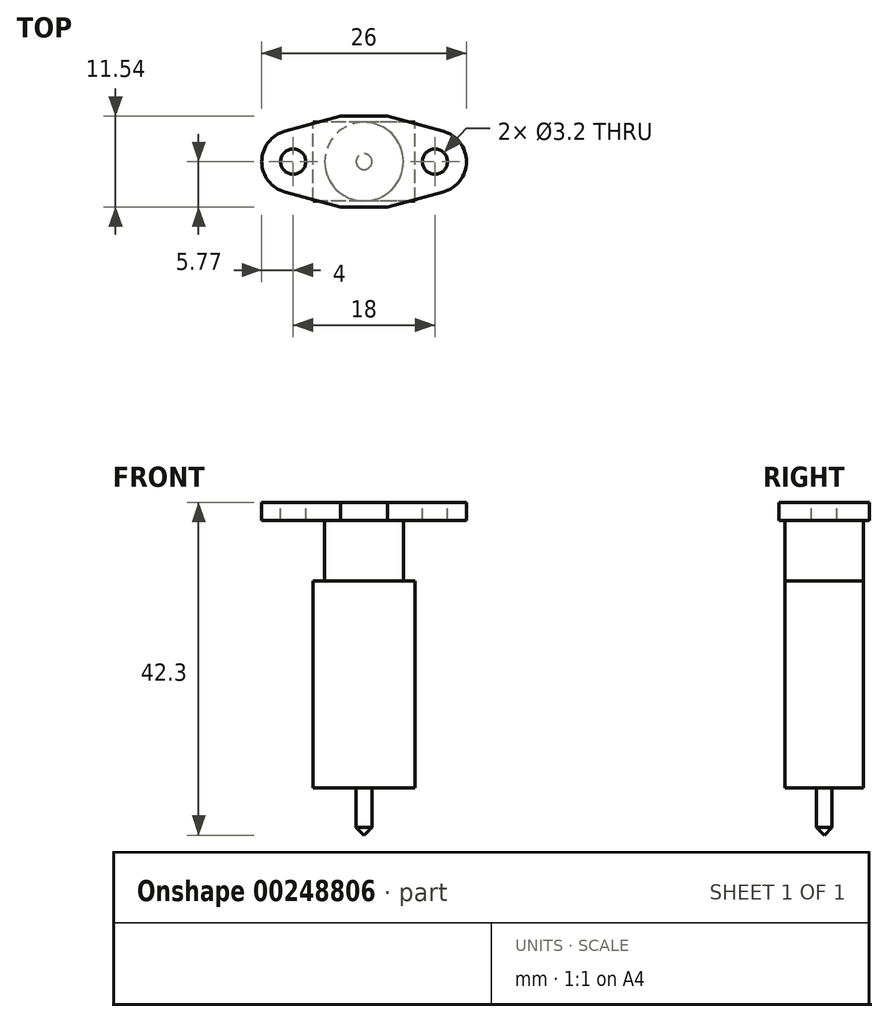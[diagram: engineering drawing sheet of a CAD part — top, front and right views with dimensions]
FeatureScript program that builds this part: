
annotation { "Feature Type Name" : "Feature", "Feature Type Description" : "" }
export const myFeature = defineFeature(function(context is Context, id is Id, definition is map)
    precondition{}
    {
        {
            var Q0;
            Q0=qCreatedBy(makeId("Top.planeOp"),FACE);
            var sketch = newSketch(context, id + "F0", { "sketchPlane" : qUnion([Q0])});
            skCircle(sketch, "E0", {"center": v(-9, 0) * mm, "radius": 1.6 * mm});
            skArc(sketch, "E1", {"start": v(-10.04, 3.86) * mm, "mid": v(-13, 0) * mm, "end": v(-10.04, -3.86) * mm});
            skLineSegment(sketch, "E2", {"start": v(0, 5.77) * mm, "end": v(-3, 5.76) * mm});
            skLineSegment(sketch, "E3.MirrorCS", {"start": v(0, -5.77) * mm, "end": v(-3, -5.77) * mm});
            skLineSegment(sketch, "E4", {"start": v(-3, 5.76) * mm, "end": v(-10.04, 3.86) * mm});
            skLineSegment(sketch, "E5.MirrorCS", {"start": v(-3, -5.76) * mm, "end": v(-10.04, -3.86) * mm});
            skLineSegment(sketch, "E6.MirrorCS", {"start": v(3, -5.76) * mm, "end": v(10.04, -3.86) * mm});
            skLineSegment(sketch, "E7.MirrorCS", {"start": v(0, -5.77) * mm, "end": v(3, -5.77) * mm});
            skCircle(sketch, "E8.MirrorC", {"center": v(9, 0) * mm, "radius": 1.6 * mm});
            skArc(sketch, "E9.MirrorCS", {"start": v(10.04, 3.86) * mm, "mid": v(13, 0) * mm, "end": v(10.04, -3.86) * mm});
            skLineSegment(sketch, "E10.MirrorCS", {"start": v(3, 5.76) * mm, "end": v(10.04, 3.86) * mm});
            skLineSegment(sketch, "E11.MirrorCS", {"start": v(0, 5.77) * mm, "end": v(3, 5.76) * mm});
            skSolve(sketch);
        }
        {
            var Q0;
            Q0=makeQuery(id+"F0.imprint","IMPRINT",FACE,{"disambiguationData":[TD([[makeQuery(id+"F0.imprint","IMPRINT",EDGE,{"derivedFrom":sQuery(id+"F0.wireOp",EDGE,"E0")}),-1.0]])]});
            extrude(context, id + "F1", {"entities" : qUnion([Q0]), "oppositeDirection" : true, "depth" : 2.3 * mm, "offsetDistance" : 25 * mm});
        }
        {
            var Q0;
            Q0=makeQuery(id+"F1.opExtrude","CAP_FACE",FACE,{"disambiguationData":[OSD([sQuery(id+"F0.wireOp",EDGE,"E0"),sQuery(id+"F0.wireOp",EDGE,"E1"),sQuery(id+"F0.wireOp",EDGE,"E2"),sQuery(id+"F0.wireOp",EDGE,"E3.MirrorCS"),sQuery(id+"F0.wireOp",EDGE,"E4"),sQuery(id+"F0.wireOp",EDGE,"E5.MirrorCS"),sQuery(id+"F0.wireOp",EDGE,"E6.MirrorCS"),sQuery(id+"F0.wireOp",EDGE,"E7.MirrorCS"),sQuery(id+"F0.wireOp",EDGE,"E8.MirrorC"),sQuery(id+"F0.wireOp",EDGE,"E9.MirrorCS"),sQuery(id+"F0.wireOp",EDGE,"E10.MirrorCS"),sQuery(id+"F0.wireOp",EDGE,"E11.MirrorCS")])],"isStart":false});
            var sketch = newSketch(context, id + "F2", { "sketchPlane" : qUnion([Q0])});
            skCircle(sketch, "E12", {"center": v(0, 0) * mm, "radius": 5 * mm});
            skSolve(sketch);
        }
        {
            var Q0;
            Q0=makeQuery(id+"F2.imprint","IMPRINT",FACE,{"disambiguationData":[TD([[makeQuery(id+"F2.imprint","IMPRINT",EDGE,{"derivedFrom":sQuery(id+"F2.wireOp",EDGE,"E12")}),1.0]])]});
            extrude(context, id + "F3", {"entities" : qUnion([Q0]), "operationType" : NewBodyOperationType.ADD, "depth" : 7.7 * mm, "offsetDistance" : 25 * mm});
        }
        {
            var Q0;
            Q0=makeQuery(id+"F3.opExtrude","CAP_FACE",FACE,{"disambiguationData":[OSD([sQuery(id+"F2.wireOp",EDGE,"E12")])],"isStart":false});
            var sketch = newSketch(context, id + "F4", { "sketchPlane" : qUnion([Q0])});
            skLineSegment(sketch, "E13.bottom", {"start": v(6.5, 5) * mm, "end": v(-6.5, 5) * mm});
            skLineSegment(sketch, "E13.top", {"start": v(6.5, -5) * mm, "end": v(-6.5, -5) * mm});
            skLineSegment(sketch, "E13.left", {"start": v(6.5, 5) * mm, "end": v(6.5, -5) * mm});
            skLineSegment(sketch, "E13.right", {"start": v(-6.5, 5) * mm, "end": v(-6.5, -5) * mm});
            skPoint(sketch, "E13.middle", {"position": v(0, 0) * mm});
            skSolve(sketch);
        }
        {
            var Q0;
            {var subQ0=sQuery(id+"F4.wireOp",EDGE,"E13.left");var subQ1=sQuery(id+"F4.wireOp",EDGE,"E13.bottom");var subQ2=makeQuery(id+"F4.imprint","INTERSECT",VERTEX,{"derivedFrom":[subQ1,subQ0]});Q0=makeQuery(id+"F4.imprint","IMPRINT",FACE,{"disambiguationData":[TD([[makeQuery(id+"F4.imprint","IMPRINT",EDGE,{"disambiguationData":[TD([[subQ2,-1.0]])],"derivedFrom":subQ1}),1.0]])]});}
            var Q1;
            {var subQ0=sQuery(id+"F4.wireOp",EDGE,"E13.right");var subQ1=sQuery(id+"F4.wireOp",EDGE,"E13.bottom");var subQ2=makeQuery(id+"F4.imprint","INTERSECT",VERTEX,{"derivedFrom":[subQ1,subQ0]});Q1=makeQuery(id+"F4.imprint","IMPRINT",FACE,{"disambiguationData":[TD([[makeQuery(id+"F4.imprint","IMPRINT",EDGE,{"disambiguationData":[TD([[subQ2,1.0]])],"derivedFrom":subQ1}),1.0]])]});}
            var Q2;
            {var subQ0=makeQuery(id+"F3.opExtrude","CAP_EDGE",EDGE,{"disambiguationData":[OSD([sQuery(id+"F2.wireOp",EDGE,"E12")])],"isStart":false});var subQ1=makeQuery(id+"F4.imprint","INTERSECT",VERTEX,{"derivedFrom":[subQ0,sQuery(id+"F4.wireOp",EDGE,"E13.bottom")]});Q2=makeQuery(id+"F4.imprint","IMPRINT",FACE,{"disambiguationData":[TD([[makeQuery(id+"F4.imprint","IMPRINT",EDGE,{"disambiguationData":[TD([[subQ1,1.0]])],"derivedFrom":subQ0}),1.0]])]});}
            var Q3;
            {var subQ0=sQuery(id+"F4.wireOp",EDGE,"E13.right");var subQ1=sQuery(id+"F4.wireOp",EDGE,"E13.top");var subQ2=makeQuery(id+"F4.imprint","INTERSECT",VERTEX,{"derivedFrom":[subQ1,subQ0]});Q3=makeQuery(id+"F4.imprint","IMPRINT",FACE,{"disambiguationData":[TD([[makeQuery(id+"F4.imprint","IMPRINT",EDGE,{"disambiguationData":[TD([[subQ2,1.0]])],"derivedFrom":subQ1}),-1.0]])]});}
            var Q4;
            {var subQ0=sQuery(id+"F4.wireOp",EDGE,"E13.left");var subQ1=sQuery(id+"F4.wireOp",EDGE,"E13.top");var subQ2=makeQuery(id+"F4.imprint","INTERSECT",VERTEX,{"derivedFrom":[subQ1,subQ0]});Q4=makeQuery(id+"F4.imprint","IMPRINT",FACE,{"disambiguationData":[TD([[makeQuery(id+"F4.imprint","IMPRINT",EDGE,{"disambiguationData":[TD([[subQ2,-1.0]])],"derivedFrom":subQ1}),-1.0]])]});}
            extrude(context, id + "F5", {"entities" : qUnion([Q0, Q1, Q2, Q3, Q4]), "operationType" : NewBodyOperationType.ADD, "depth" : 26.3 * mm, "offsetDistance" : 25 * mm});
        }
        {
            var Q0;
            Q0=makeQuery(id+"F5.opExtrude","CAP_FACE",FACE,{"disambiguationData":[OSD([sQuery(id+"F4.wireOp",EDGE,"E13.bottom"),sQuery(id+"F4.wireOp",EDGE,"E13.top"),sQuery(id+"F4.wireOp",EDGE,"E13.left"),sQuery(id+"F4.wireOp",EDGE,"E13.right")])],"isStart":false});
            var sketch = newSketch(context, id + "F6", { "sketchPlane" : qUnion([Q0])});
            skCircle(sketch, "E14", {"center": v(0, 0) * mm, "radius": 1 * mm});
            skSolve(sketch);
        }
        {
            var Q0;
            Q0=makeQuery(id+"F6.imprint","IMPRINT",FACE,{"disambiguationData":[TD([[makeQuery(id+"F6.imprint","IMPRINT",EDGE,{"derivedFrom":sQuery(id+"F6.wireOp",EDGE,"E14")}),1.0]])]});
            extrude(context, id + "F7", {"entities" : qUnion([Q0]), "operationType" : NewBodyOperationType.ADD, "depth" : 6 * mm, "offsetDistance" : 25 * mm});
        }
        {
            var Q0;
            Q0=makeQuery(id+"F7.opExtrude","CAP_EDGE",EDGE,{"disambiguationData":[OSD([sQuery(id+"F6.wireOp",EDGE,"E14")])],"isStart":false});
            chamfer(context, id + "F8", {"entities" : qUnion([Q0]), "width" : 1 * mm, "tangentPropagation" : true});
        }
    });
